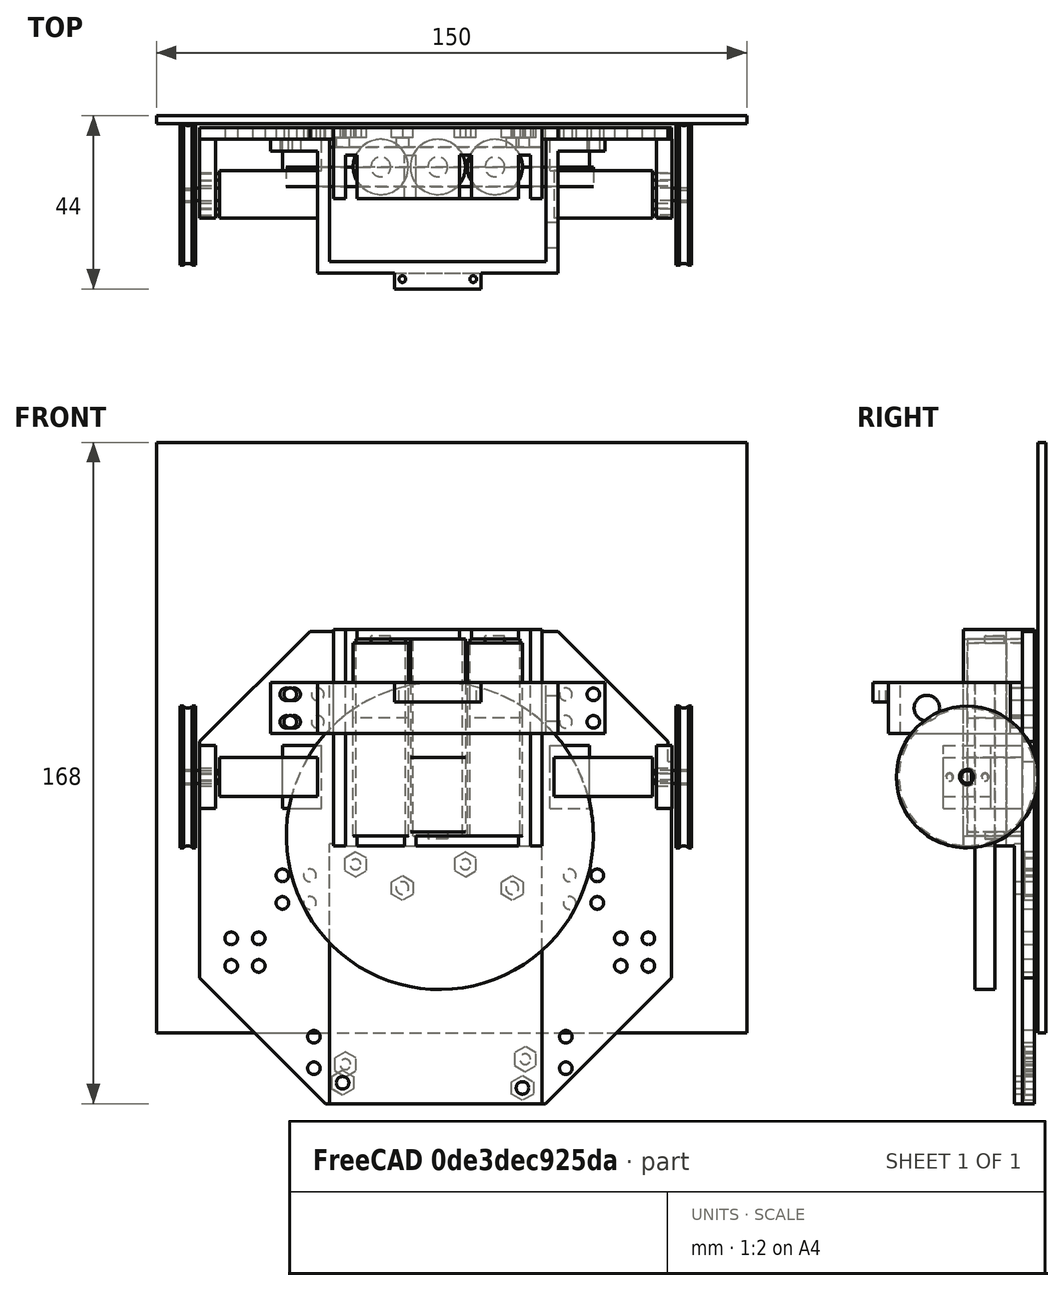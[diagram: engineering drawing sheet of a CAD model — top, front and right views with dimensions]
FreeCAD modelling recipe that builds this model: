
FCSTD DOCUMENT  (FreeCAD 0.16R6712 (Git))
Label: 5028.1 Frank the Robot
License: All rights reserved
LicenseURL: http://en.wikipedia.org/wiki/All_rights_reserved
objects: Part::Cylinder×52, Part::Cut×44, Part::Fuse×31, Part::Box×26, Part::MultiFuse×10, Part::Mirroring×5, Part::Chamfer×4, Part::Compound×3, Part::Torus×2
note: 177 computed .brp shape members not serialized (recipe doc carries the construction recipe); baked Part::Feature solids carry a one-line shape summary decoded from their .brp

FEATURE [Part::Cylinder] Cylinder
  Angle = 360
  Height = 30
  Radius = 7
FEATURE [Part::Cylinder] Cylinder001
  Angle = 360
  Height = 19
  Placement = pos=(0,0,30) rot=(0,0,1;0rad)
  Radius = 7
FEATURE [Part::Cylinder] Cylinder002
  Angle = 360
  Height = 1.8
  Placement = pos=(0,0,49) rot=(0,0,1;0rad)
  Radius = 2.5
FEATURE [Part::Compound] Compound
  Links = -> [Cylinder,Cylinder002,Cylinder001]
FEATURE [Part::Cylinder] Cylinder003
  Angle = 360
  Height = 30
  Radius = 7
FEATURE [Part::Cylinder] Cylinder004
  Angle = 360
  Height = 19
  Placement = pos=(0,0,30) rot=(0,0,1;0rad)
  Radius = 7
FEATURE [Part::Cylinder] Cylinder005
  Angle = 360
  Height = 1.8
  Placement = pos=(0,0,49) rot=(0,0,1;0rad)
  Radius = 2.5
FEATURE [Part::Compound] Compound001
  Links = -> [Cylinder003,Cylinder005,Cylinder004]
  Placement = pos=(14.5,0,50) rot=(1,0,0;3.14159rad)
FEATURE [Part::Cylinder] Cylinder006
  Angle = 360
  Height = 30
  Radius = 7
FEATURE [Part::Cylinder] Cylinder007
  Angle = 360
  Height = 19
  Placement = pos=(0,0,30) rot=(0,0,1;0rad)
  Radius = 7
FEATURE [Part::Cylinder] Cylinder008
  Angle = 360
  Height = 1.8
  Placement = pos=(0,0,49) rot=(0,0,1;0rad)
  Radius = 2.5
FEATURE [Part::Compound] Compound002
  Links = -> [Cylinder006,Cylinder008,Cylinder007]
  Placement = pos=(29,0,0) rot=(0,0,1;0rad)
FEATURE [Part::Box] Box  label="Cube"
  Height = 50
  Length = 47
  Placement = pos=(-9,-8,0) rot=(0,0,1;0rad)
  Width = 12
FEATURE [Part::Box] Box001  label="Cube001"
  Height = 55
  Length = 53
  Placement = pos=(-12,-8,-2.5) rot=(0,0,1;0rad)
  Width = 11
FEATURE [Part::Cylinder] Cylinder009
  Angle = 360
  Height = 50
  Radius = 7
FEATURE [Part::Cylinder] Cylinder010
  Angle = 360
  Height = 50
  Placement = pos=(14.5,0,0) rot=(0,0,1;0rad)
  Radius = 7
FEATURE [Part::Cut] Cut
  Base = -> Box001
  Tool = -> Box
FEATURE [Part::Box] Box002  label="Cube002"
  Height = 55
  Length = 53
  Placement = pos=(-12,3,-2.5) rot=(0,0,1;0rad)
  Width = 7
FEATURE [Part::Fuse] Fusion
  Base = -> Cut
  Tool = -> Box002
FEATURE [Part::Cut] Cut001
  Base = -> Fusion
  Tool = -> Cylinder009
FEATURE [Part::Cut] Cut002
  Base = -> Cut001
  Tool = -> Cylinder010
FEATURE [Part::Cylinder] Cylinder011
  Angle = 360
  Height = 50
  Placement = pos=(29,0,0) rot=(0,0,1;0rad)
  Radius = 7
FEATURE [Part::Cut] Cut003
  Base = -> Cut002
  Tool = -> Cylinder011
FEATURE [Part::Box] Box003  label="Cube003"
  Height = 5
  Length = 3
  Placement = pos=(6,-9,-4) rot=(0,0,1;0rad)
  Width = 12
FEATURE [Part::Cut] Cut004
  Base = -> Cut003
  Tool = -> Box003
FEATURE [Part::Box] Box004  label="Cube004"
  Height = 5
  Length = 3
  Placement = pos=(20,-9,48) rot=(0,0,1;0rad)
  Width = 12
FEATURE [Part::Cut] Cut005
  Base = -> Cut004
  Tool = -> Box004
FEATURE [Part::Box] Box005  label="Cube005"
  Height = 5
  Length = 3
  Placement = pos=(-9,-9,48) rot=(0,0,1;0rad)
  Width = 12
FEATURE [Part::Cut] Cut006
  Base = -> Cut005
  Tool = -> Box005
FEATURE [Part::Box] Box006  label="Cube006"
  Height = 5
  Length = 3
  Placement = pos=(35,-9,-4) rot=(0,0,1;0rad)
  Width = 12
FEATURE [Part::Cut] Cut007
  Base = -> Cut006
  Tool = -> Box006
FEATURE [Part::Cut] Cut008
FEATURE [Part::Torus] Torus001
  Angle1 = -180
  Angle2 = 180
  Angle3 = 360
  Placement = pos=(0,0,2) rot=(0,0,1;0rad)
  Radius1 = 19
  Radius2 = 1.5
FEATURE [Part::Cut] Cut009  label="wheel2"
  Base = -> Cut008
  Placement = pos=(75,-7,15) rot=(0,1,0;1.5708rad)
  Tool = -> Torus001
FEATURE [Part::Torus] Torus
  Angle1 = -180
  Angle2 = 180
  Angle3 = 360
  Placement = pos=(0,0,2) rot=(0,0,1;0rad)
  Radius1 = 19
  Radius2 = 1.5
FEATURE [Part::Cut] Cut010
FEATURE [Part::Cut] Cut011  label="wheel1"
  Base = -> Cut010
  Placement = pos=(-51,-7,15) rot=(0,1,0;1.5708rad)
  Tool = -> Torus
FEATURE [Part::Fuse] Fusion003
FEATURE [Part::Cylinder] Cylinder012
  Angle = 360
  Height = 10
  Placement = pos=(5,-4.5,0) rot=(0,1,0;1.5708rad)
  Radius = 0.8
FEATURE [Part::Fuse] Fusion048  label="right-motor001"
  Base = -> Cylinder012
  Placement = pos=(-51,-7,15) rot=(0,0,1;0rad)
  Tool = -> Fusion003
FEATURE [Part::Fuse] Fusion049
FEATURE [Part::Cylinder] Cylinder013
  Angle = 360
  Height = 10
  Placement = pos=(5,-4.5,0) rot=(0,1,0;1.5708rad)
  Radius = 0.8
FEATURE [Part::Fuse] Fusion050  label="left-motor001"
  Base = -> Cylinder013
  Placement = pos=(79,-7,15) rot=(0,0,1;3.14159rad)
  Tool = -> Fusion049
FEATURE [Part::Box] Box007  label="Cube007"
  Height = 5
  Length = 3
  Placement = pos=(35,-9,49) rot=(0,0,1;0rad)
  Width = 12
FEATURE [Part::Cut] Cut012
  Base = -> Cut007
  Tool = -> Box007
FEATURE [Part::Box] Box008  label="Cube008"
  Height = 5
  Length = 3
  Placement = pos=(-9,-9,-4) rot=(0,0,1;0rad)
  Width = 12
FEATURE [Part::Cut] Cut013  label="Batt Holder"
  Base = -> Cut012
  Tool = -> Box008
FEATURE [Part::Box] Box009  label="The Ground"
  Height = 150
  Length = 150
  Placement = pos=(-57,11,-50) rot=(0,0,1;0rad)
  Width = 2
FEATURE [Part::Box] Box010  label="Cube009"
  Height = 16
  Length = 4
  Placement = pos=(70,-13,7) rot=(0,0,1;0rad)
  Width = 20
FEATURE [Part::Box] Box011  label="Cube010"
  Height = 16
  Length = 4
  Placement = pos=(-46,-13,7) rot=(0,0,1;0rad)
  Width = 20
FEATURE [Part::Box] Box012  label="Cube011"
  Height = 16
  Length = 10
  Placement = pos=(-25,-1,7) rot=(0,0,1;0rad)
  Width = 8
FEATURE [Part::Box] Box013  label="Cube012"
  Height = 16
  Length = 10
  Placement = pos=(43,-1,7) rot=(0,0,1;0rad)
  Width = 8
FEATURE [Part::Cylinder] Cylinder014
  Angle = 360
  Height = 28
  Placement = pos=(40.7,0,-10.3) rot=(1,0,0;1.5708rad)
  Radius = 1.6
FEATURE [Part::Cylinder] Cylinder015
  Angle = 360
  Height = 28
  Placement = pos=(-2.4,0,-59.8) rot=(1,0,0;1.5708rad)
  Radius = 1.6
FEATURE [Part::Cylinder] Cylinder016
  Angle = 360
  Height = 28
  Placement = pos=(-5,0,-9) rot=(1,0,0;1.5708rad)
  Radius = 1.6
FEATURE [Part::Cylinder] Cylinder017
  Angle = 360
  Height = 28
  Placement = pos=(25.5,0,-59.8) rot=(1,0,0;1.5708rad)
  Radius = 1.6
FEATURE [Part::Fuse] Fusion051
  Base = -> Cylinder015
  Tool = -> Cylinder016
FEATURE [Part::Fuse] Fusion052
  Base = -> Cylinder014
  Tool = -> Cylinder017
FEATURE [Part::Fuse] Fusion053  label="Screw holes on Arduino Duo"
  Base = -> Fusion051
  Tool = -> Fusion052
FEATURE [Part::Mirroring] Part__Mirroring  label="XXXXXScrew holes on Arduino Duo (Mirror #1)"
  Base = (0,0,0)
  Normal = (0,0,1)
  Placement = pos=(-204,10,-67) rot=(0,0,1;0rad)
  Source = -> Fusion053
FEATURE [Part::Box] Box014  label="Cube013"
  Height = 45
  Length = 119
  Placement = pos=(-46,7,7) rot=(0,0,1;0rad)
  Width = 3
FEATURE [Part::Box] Box015  label="Cube014"
  Height = 66
  Length = 54
  Placement = pos=(-13,5,-68) rot=(0,0,1;0rad)
  Width = 5
FEATURE [Part::Cylinder] Cylinder018
  Angle = 360
  Height = 5
  Placement = pos=(15,0,0) rot=(1,0,0;1.5708rad)
  Radius = 39
FEATURE [Part::Cut] Cut014  label="M3 Nut"
  Base = -> Cut001
  Placement = pos=(-6.4,10,-7.2) rot=(1,0,0;1.5708rad)
  Tool = -> Cylinder001
FEATURE [Part::Cut] Cut015  label="M3 Nut001"
  Base = -> Cut001
  Placement = pos=(21.5,10,-7.2) rot=(1,0,0;1.5708rad)
  Tool = -> Cylinder001
FEATURE [Part::Cut] Cut016  label="M3 Nut002"
  Base = -> Cut001
  Placement = pos=(36.7,10,-56.7) rot=(1,0,0;1.5708rad)
  Tool = -> Cylinder001
FEATURE [Part::Cut] Cut017  label="M3 Nut003"
  Base = -> Cut001
  Placement = pos=(-9,10,-58) rot=(1,0,0;1.5708rad)
  Tool = -> Cylinder001
FEATURE [Part::Cut] Cut018
  Base = -> Cut
  Placement = pos=(-9,10,-58) rot=(1,0,0;1.5708rad)
  Tool = -> Box006
FEATURE [Part::Cut] Cut019
  Base = -> Cut
  Placement = pos=(36.7,10,-56.7) rot=(1,0,0;1.5708rad)
  Tool = -> Box006
FEATURE [Part::Cut] Cut020
  Base = -> Cut
  Placement = pos=(-6.4,10,-7.2) rot=(1,0,0;1.5708rad)
  Tool = -> Box006
FEATURE [Part::Cut] Cut021
  Base = -> Cut
  Placement = pos=(21.5,10,-7.2) rot=(1,0,0;1.5708rad)
  Tool = -> Box006
FEATURE [Part::MultiFuse] Fusion054  label="XXXXXHex Holes"
  Placement = pos=(200,0,0) rot=(0,0,1;0rad)
  Shapes = -> [Cut018,Cut021,Cut019,Cut020]
FEATURE [Part::Cut] Cut022
  Base = -> Box015
  Tool = -> Fusion054
FEATURE [Part::Cut] Cut023
  Base = -> Cut022
  Tool = -> Part__Mirroring
FEATURE [Part::Chamfer] Chamfer
  Base = -> Box014
  Edges = 1 edges r=28: [Edge2]
FEATURE [Part::Chamfer] Chamfer001
  Base = -> Chamfer
  Edges = 1 edges r=28: [Edge15]
FEATURE [Part::Box] Box016  label="Cube015"
  Height = 87
  Length = 34
  Placement = pos=(-46,7,-68) rot=(0,0,1;0rad)
  Width = 3
FEATURE [Part::Chamfer] Chamfer002
  Base = -> Box016
  Edges = 1 edges r=32: [Edge4]
FEATURE [Part::Box] Box017  label="Cube016"
  Height = 87
  Length = 33.7
  Placement = pos=(40.2,7,-68) rot=(0,0,1;0rad)
  Width = 3
FEATURE [Part::Chamfer] Chamfer003
  Base = -> Box017
  Edges = 1 edges r=32: [Edge8]
FEATURE [Part::Cylinder] Cylinder019
  Angle = 360
  Height = 28
  Placement = pos=(48,20,-10) rot=(1,0,0;1.5708rad)
  Radius = 1.6
FEATURE [Part::Cylinder] Cylinder020
  Angle = 360
  Height = 28
  Placement = pos=(47,20,-51) rot=(1,0,0;1.5708rad)
  Radius = 1.6
FEATURE [Part::Cylinder] Cylinder021
  Angle = 360
  Height = 28
  Placement = pos=(48,20,-17) rot=(1,0,0;1.5708rad)
  Radius = 1.6
FEATURE [Part::Cylinder] Cylinder022
  Angle = 360
  Height = 28
  Placement = pos=(47,20,-59) rot=(1,0,0;1.5708rad)
  Radius = 1.6
FEATURE [Part::Cylinder] Cylinder023
  Angle = 360
  Height = 28
  Placement = pos=(55,20,-17) rot=(1,0,0;1.5708rad)
  Radius = 1.6
FEATURE [Part::Cylinder] Cylinder024
  Angle = 360
  Height = 28
  Placement = pos=(55,20,-10) rot=(1,0,0;1.5708rad)
  Radius = 1.6
FEATURE [Part::MultiFuse] Fusion055
  Shapes = -> [Cylinder021,Cylinder023,Cylinder024,Cylinder019]
FEATURE [Part::MultiFuse] Fusion056
  Placement = pos=(13,0,-16) rot=(0,0,1;0rad)
  Shapes = -> [Cylinder021,Cylinder023,Cylinder024,Cylinder019]
FEATURE [Part::MultiFuse] Fusion057  label="Mount holes top left"
  Placement = pos=(-1,0,46) rot=(0,0,1;0rad)
  Shapes = -> [Cylinder021,Cylinder023,Cylinder024,Cylinder019]
FEATURE [Part::MultiFuse] Fusion058  label="Mount holes top right"
  Placement = pos=(-71,0,46) rot=(0,0,1;0rad)
  Shapes = -> [Cylinder021,Cylinder023,Cylinder024,Cylinder019]
FEATURE [Part::MultiFuse] Fusion059
  Shapes = -> [Cylinder022,Cylinder020,Fusion055,Fusion056]
FEATURE [Part::Mirroring] Part__Mirroring001  label="Mount holes bottom right"
  Base = (0,0,0)
  Normal = (1,0,0)
  Placement = pos=(30,0,0) rot=(0,0,1;0rad)
  Source = -> Fusion059
FEATURE [Part::Cylinder] Cylinder025
  Angle = 360
  Height = 28
  Placement = pos=(48,20,-10) rot=(1,0,0;1.5708rad)
  Radius = 1.6
FEATURE [Part::Cylinder] Cylinder026
  Angle = 360
  Height = 28
  Placement = pos=(47,20,-51) rot=(1,0,0;1.5708rad)
  Radius = 1.6
FEATURE [Part::Cylinder] Cylinder027
  Angle = 360
  Height = 28
  Placement = pos=(48,20,-17) rot=(1,0,0;1.5708rad)
  Radius = 1.6
FEATURE [Part::Cylinder] Cylinder028
  Angle = 360
  Height = 28
  Placement = pos=(47,20,-59) rot=(1,0,0;1.5708rad)
  Radius = 1.6
FEATURE [Part::Cylinder] Cylinder029
  Angle = 360
  Height = 28
  Placement = pos=(55,20,-17) rot=(1,0,0;1.5708rad)
  Radius = 1.6
FEATURE [Part::Cylinder] Cylinder030
  Angle = 360
  Height = 28
  Placement = pos=(55,20,-10) rot=(1,0,0;1.5708rad)
  Radius = 1.6
FEATURE [Part::MultiFuse] Fusion060
  Shapes = -> [Cylinder027,Cylinder029,Cylinder030,Cylinder025]
FEATURE [Part::MultiFuse] Fusion061
  Placement = pos=(13,0,-16) rot=(0,0,1;0rad)
  Shapes = -> [Cylinder027,Cylinder029,Cylinder030,Cylinder025]
FEATURE [Part::MultiFuse] Fusion062  label="Mount holes bottom left"
  Shapes = -> [Cylinder028,Cylinder026,Fusion060,Fusion061]
FEATURE [Part::Fuse] Fusion063
  Base = -> Chamfer001
  Tool = -> Chamfer002
FEATURE [Part::Fuse] Fusion064
  Base = -> Chamfer003
  Tool = -> Fusion063
FEATURE [Part::Fuse] Fusion065
  Base = -> Cut023
  Tool = -> Fusion064
FEATURE [Part::Fuse] Fusion066
  Base = -> Box010
  Tool = -> Fusion065
FEATURE [Part::Fuse] Fusion067
  Base = -> Box011
  Tool = -> Fusion066
FEATURE [Part::Fuse] Fusion068
  Base = -> Box012
  Tool = -> Fusion067
FEATURE [Part::Fuse] Fusion069
  Base = -> Box013
  Tool = -> Fusion068
FEATURE [Part::Fuse] Fusion070
  Base = -> Cut013
  Tool = -> Fusion069
FEATURE [Part::Cut] Cut024
  Base = -> Fusion070
  Tool = -> Fusion062
FEATURE [Part::Cut] Cut025
  Base = -> Cut024
  Tool = -> Part__Mirroring001
FEATURE [Part::Cut] Cut026
  Base = -> Cut025
  Tool = -> Fusion058
FEATURE [Part::Cut] Cut027
  Base = -> Cut026
  Tool = -> Fusion057
FEATURE [Part::Cylinder] Cylinder031  label="Cylinder041"
  Angle = 360
  Height = 10
  Placement = pos=(0,18,29) rot=(0,0,1;0rad)
  Radius = 2.25
FEATURE [Part::Cylinder] Cylinder032  label="Cylinder042"
  Angle = 360
  Height = 10
  Placement = pos=(4.5,18,32) rot=(0,0,1;0rad)
  Radius = 1
FEATURE [Part::Cylinder] Cylinder033  label="Cylinder043"
  Angle = 360
  Height = 10
  Placement = pos=(-4.5,18,32) rot=(0,0,1;0rad)
  Radius = 1
FEATURE [Part::Fuse] Fusion009  label="Mounting Screw Holes"
  Base = -> Cylinder032
  Tool = -> Cylinder033
FEATURE [Part::Fuse] Fusion071  label="Motor Holes Left"
  Base = -> Cylinder031
  Placement = pos=(37,-7,-3) rot=(0.57735,0.57735,0.57735;2.0944rad)
  Tool = -> Fusion009
FEATURE [Part::Cut] Cut028
  Base = -> Cut027
  Tool = -> Fusion071
FEATURE [Part::Cylinder] Cylinder034  label="Cylinder044"
  Angle = 360
  Height = 10
  Placement = pos=(0,18,29) rot=(0,0,1;0rad)
  Radius = 2.25
FEATURE [Part::Cylinder] Cylinder035  label="Cylinder045"
  Angle = 360
  Height = 10
  Placement = pos=(4.5,18,32) rot=(0,0,1;0rad)
  Radius = 1
FEATURE [Part::Cylinder] Cylinder036  label="Cylinder046"
  Angle = 360
  Height = 10
  Placement = pos=(-4.5,18,32) rot=(0,0,1;0rad)
  Radius = 1
FEATURE [Part::Fuse] Fusion072  label="Mounting Screw Holes001"
  Base = -> Cylinder035
  Tool = -> Cylinder036
FEATURE [Part::Fuse] Fusion073  label="Motor Holes Right"
  Base = -> Cylinder034
  Placement = pos=(-79,-7,-3) rot=(0.57735,0.57735,0.57735;2.0944rad)
  Tool = -> Fusion072
FEATURE [Part::Cut] Cut029
  Base = -> Cut028
  Tool = -> Fusion073
FEATURE [Part::Cylinder] Cylinder037  label="Cylinder047"
  Angle = 360
  Height = 28
  Placement = pos=(40.7,0,-10.3) rot=(1,0,0;1.5708rad)
  Radius = 1.6
FEATURE [Part::Cylinder] Cylinder038  label="Cylinder048"
  Angle = 360
  Height = 28
  Placement = pos=(-2.4,0,-59.8) rot=(1,0,0;1.5708rad)
  Radius = 1.6
FEATURE [Part::Cylinder] Cylinder039  label="Cylinder049"
  Angle = 360
  Height = 28
  Placement = pos=(-5,0,-9) rot=(1,0,0;1.5708rad)
  Radius = 1.6
FEATURE [Part::Cylinder] Cylinder040  label="Cylinder050"
  Angle = 360
  Height = 28
  Placement = pos=(25.5,0,-59.8) rot=(1,0,0;1.5708rad)
  Radius = 1.6
FEATURE [Part::Fuse] Fusion074
  Base = -> Cylinder038
  Tool = -> Cylinder039
FEATURE [Part::Fuse] Fusion075
  Base = -> Cylinder037
  Tool = -> Cylinder040
FEATURE [Part::Fuse] Fusion076  label="Screw holes on Arduino Duo001"
  Base = -> Fusion074
  Tool = -> Fusion075
FEATURE [Part::Mirroring] Part__Mirroring002  label="Screw holes on Arduino Duo (Mirror #1)001"
  Base = (0,0,0)
  Normal = (0,0,1)
  Placement = pos=(-4,10,-67) rot=(0,0,1;0rad)
  Source = -> Fusion076
FEATURE [Part::Mirroring] Part__Mirroring003  label="Screw holes on Arduino Duo (Mirror #1)001 (Mirror #4)"
  Base = (0,0,0)
  Normal = (1,0,0)
  Placement = pos=(27,0,-6) rot=(0,0,1;0rad)
  Source = -> Part__Mirroring002
FEATURE [Part::Cut] Cut030
  Base = -> Cut029
  Tool = -> Part__Mirroring003
FEATURE [Part::Box] Box018  label="Cube017"
  Height = 50
  Length = 47
  Placement = pos=(-9,-8,0) rot=(0,0,1;0rad)
  Width = 12
FEATURE [Part::Box] Box019  label="Cube018"
  Height = 55
  Length = 53
  Placement = pos=(-12,-8,-2.5) rot=(0,0,1;0rad)
  Width = 11
FEATURE [Part::Cut] Cut031
  Base = -> Box019
  Tool = -> Box018
FEATURE [Part::Box] Box020  label="Cube019"
  Height = 5
  Length = 3
  Placement = pos=(35,-9,-4) rot=(0,0,1;0rad)
  Width = 12
FEATURE [Part::Cut] Cut032
  Base = -> Cut031
  Placement = pos=(-9,10,-58) rot=(1,0,0;1.5708rad)
  Tool = -> Box020
FEATURE [Part::Cut] Cut033
  Base = -> Cut031
  Placement = pos=(36.7,10,-56.7) rot=(1,0,0;1.5708rad)
  Tool = -> Box020
FEATURE [Part::Cut] Cut034
  Base = -> Cut031
  Placement = pos=(-6.4,10,-7.2) rot=(1,0,0;1.5708rad)
  Tool = -> Box020
FEATURE [Part::Cut] Cut035
  Base = -> Cut031
  Placement = pos=(21.5,10,-7.2) rot=(1,0,0;1.5708rad)
  Tool = -> Box020
FEATURE [Part::MultiFuse] Fusion077
  Shapes = -> [Cut032,Cut035,Cut033,Cut034]
FEATURE [Part::Mirroring] Part__Mirroring004  label="Hex Holes"
  Base = (0,0,0)
  Normal = (1,0,0)
  Placement = pos=(27,0,-6) rot=(0,0,1;0rad)
  Source = -> Fusion077
FEATURE [Part::Cut] Cut036
  Base = -> Cut030
  Tool = -> Part__Mirroring004
FEATURE [Part::Box] Box021  label="Cube020"
  Height = 13
  Length = 61
  Placement = pos=(-16,-27,26) rot=(0,0,1;0rad)
  Width = 34
FEATURE [Part::Box] Box022  label="Cube021"
  Height = 13
  Length = 12
  Placement = pos=(45,4,26) rot=(0,0,1;0rad)
  Width = 3
FEATURE [Part::Box] Box023  label="Cube022"
  Height = 13
  Length = 12
  Placement = pos=(-28,4,26) rot=(0,0,1;0rad)
  Width = 3
FEATURE [Part::Box] Box024  label="Cube023"
  Height = 13
  Length = 55
  Placement = pos=(-13,-24,26) rot=(0,0,1;0rad)
  Width = 31
FEATURE [Part::Cylinder] Cylinder041  label="Cylinder051"
  Angle = 360
  Height = 28
  Placement = pos=(54,20,29) rot=(1,0,0;1.5708rad)
  Radius = 1.6
FEATURE [Part::Cylinder] Cylinder042  label="Cylinder052"
  Angle = 360
  Height = 28
  Placement = pos=(54,20,36) rot=(1,0,0;1.5708rad)
  Radius = 1.6
FEATURE [Part::Cylinder] Cylinder043  label="Cylinder053"
  Angle = 360
  Height = 28
  Placement = pos=(-23,20,29) rot=(1,0,0;1.5708rad)
  Radius = 1.6
FEATURE [Part::Cylinder] Cylinder044  label="Cylinder054"
  Angle = 360
  Height = 28
  Placement = pos=(-23,20,36) rot=(1,0,0;1.5708rad)
  Radius = 1.6
FEATURE [Part::Cylinder] Cylinder045  label="Cylinder055"
  Angle = 360
  Height = 10
  Placement = pos=(36,-17.25,32.5) rot=(0,1,0;1.5708rad)
  Radius = 3.25
FEATURE [Part::Cut] Cut037
  Base = -> Box021
  Tool = -> Box024
FEATURE [Part::Cut] Cut038
  Base = -> Cut037
  Tool = -> Cylinder045
FEATURE [Part::Box] Box025  label="Cube024"
  Height = 5
  Length = 22
  Placement = pos=(3.5,-31,34) rot=(0,0,1;0rad)
  Width = 4
FEATURE [Part::Cylinder] Cylinder046  label="Cylinder058"
  Angle = 360
  Height = 10
  Placement = pos=(10.5,9,0) rot=(0,0,1;0rad)
  Radius = 0.85
FEATURE [Part::Cylinder] Cylinder047  label="Cylinder059"
  Angle = 360
  Height = 10
  Placement = pos=(10.5,-9,0) rot=(0,0,1;0rad)
  Radius = 0.85
FEATURE [Part::Fuse] Fusion078
  Base = -> Cylinder046
  Placement = pos=(14.5,-39,31) rot=(0,0,1;1.5708rad)
  Tool = -> Cylinder047
FEATURE [Part::Cut] Cut039
  Base = -> Box025
  Tool = -> Fusion078
FEATURE [Part::Fuse] Fusion079
  Base = -> Cut038
  Tool = -> Cut039
FEATURE [Part::Fuse] Fusion080
  Base = -> Cylinder043
  Tool = -> Cylinder044
FEATURE [Part::Fuse] Fusion081
  Base = -> Cylinder041
  Tool = -> Cylinder042
FEATURE [Part::Fuse] Fusion082
  Base = -> Box023
  Tool = -> Fusion079
FEATURE [Part::Fuse] Fusion083
  Base = -> Box022
  Tool = -> Fusion082
FEATURE [Part::Cut] Cut040
  Base = -> Fusion083
  Tool = -> Fusion081
FEATURE [Part::Cut] Cut041  label="Switch Bracket"
  Base = -> Cut040
  Tool = -> Fusion080
FEATURE [Part::Cylinder] Cylinder048  label="Cylinder062"
  Angle = 360
  Height = 28
  Placement = pos=(-23,20,29) rot=(1,0,0;1.5708rad)
  Radius = 1.6
FEATURE [Part::Cylinder] Cylinder049  label="Cylinder063"
  Angle = 360
  Height = 28
  Placement = pos=(-23,20,36) rot=(1,0,0;1.5708rad)
  Radius = 1.6
FEATURE [Part::Fuse] Fusion084
  Base = -> Cylinder048
  Placement = pos=(1,0,0) rot=(0,0,1;0rad)
  Tool = -> Cylinder049
FEATURE [Part::Cylinder] Cylinder050  label="Cylinder066"
  Angle = 360
  Height = 28
  Placement = pos=(-23,20,29) rot=(1,0,0;1.5708rad)
  Radius = 1.6
FEATURE [Part::Cylinder] Cylinder051  label="Cylinder067"
  Angle = 360
  Height = 28
  Placement = pos=(-23,20,36) rot=(1,0,0;1.5708rad)
  Radius = 1.6
FEATURE [Part::Fuse] Fusion085
  Base = -> Cylinder050
  Placement = pos=(-1,0,0) rot=(0,0,1;0rad)
  Tool = -> Cylinder051
FEATURE [Part::Cut] Cut042
  Base = -> Cut041
  Tool = -> Fusion084
FEATURE [Part::Cut] Cut043  label="Switch Bracket001"
  Base = -> Cut042
  Tool = -> Fusion085
